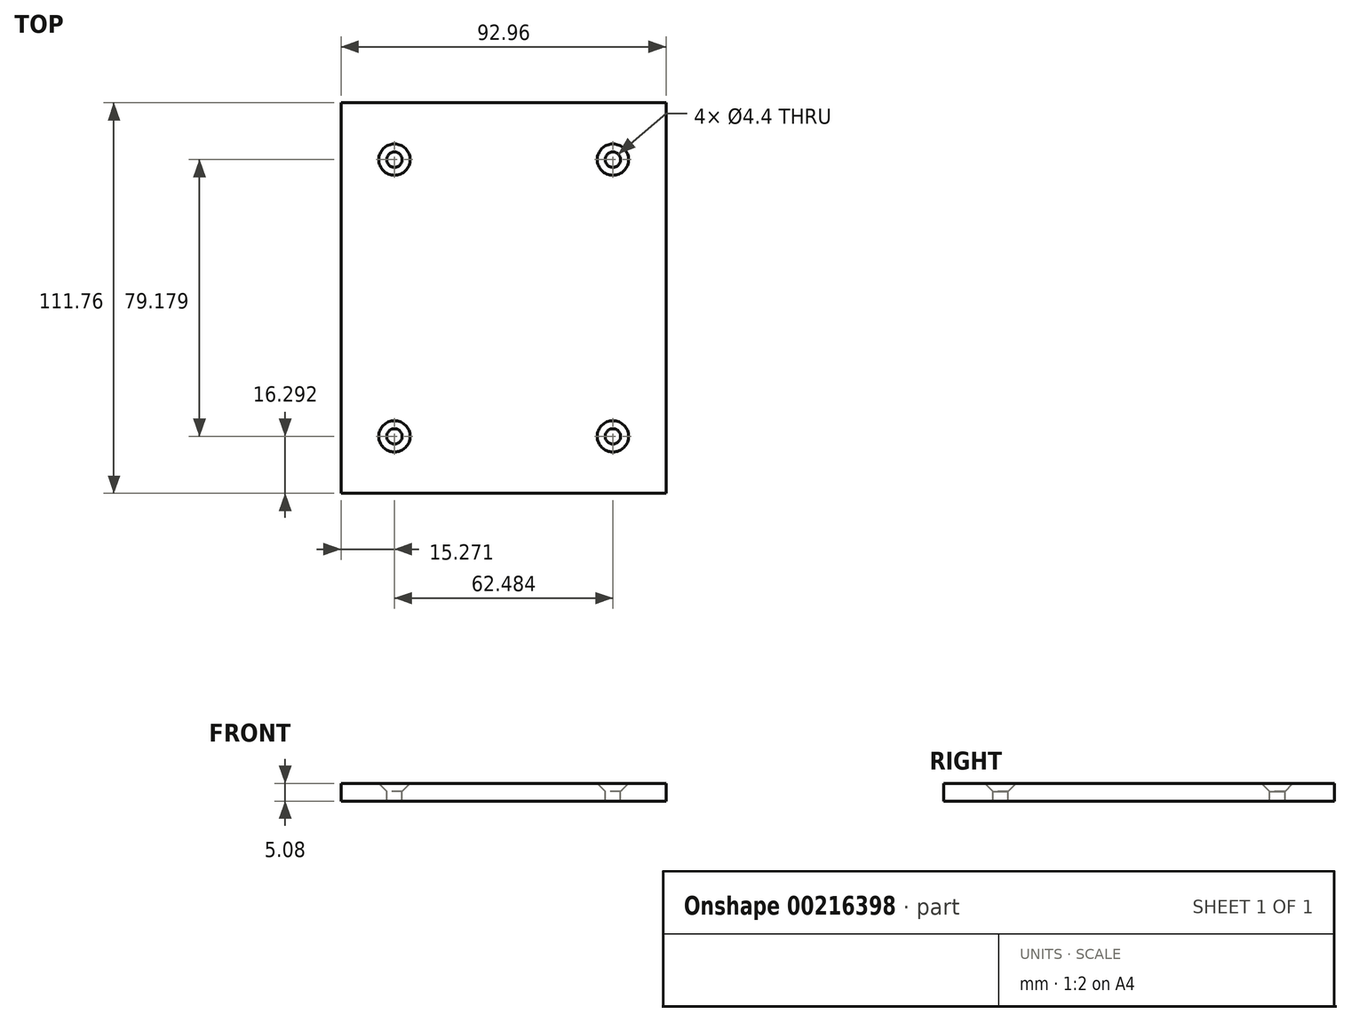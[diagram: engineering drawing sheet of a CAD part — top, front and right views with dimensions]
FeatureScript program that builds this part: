
annotation { "Feature Type Name" : "Feature", "Feature Type Description" : "" }
export const myFeature = defineFeature(function(context is Context, id is Id, definition is map)
    precondition{}
    {
        {
            var Q0;
            Q0=qCreatedBy(makeId("Top.planeOp"),FACE);
            var sketch = newSketch(context, id + "F0", { "sketchPlane" : qUnion([Q0])});
            skLineSegment(sketch, "E0.bottom", {"start": v(-46.48, 55.88) * mm, "end": v(46.48, 55.88) * mm});
            skLineSegment(sketch, "E0.top", {"start": v(-46.48, -55.88) * mm, "end": v(46.48, -55.88) * mm});
            skLineSegment(sketch, "E0.left", {"start": v(-46.48, 55.88) * mm, "end": v(-46.48, -55.88) * mm});
            skLineSegment(sketch, "E0.right", {"start": v(46.48, 55.88) * mm, "end": v(46.48, -55.88) * mm});
            skPoint(sketch, "E0.middle", {"position": v(0, 0) * mm});
            skSolve(sketch);
        }
        {
            var Q0;
            Q0 = qSketchRegion(id + "F0", true);
            extrude(context, id + "F1", {"entities" : qUnion([Q0]), "depth" : 5.08 * mm});
        }
        {
            var Q0;
            Q0=makeQuery(id+"F1.opExtrude","CAP_FACE",FACE,{"disambiguationData":[OSD([sQuery(id+"F0.wireOp",EDGE,"E0.bottom"),sQuery(id+"F0.wireOp",EDGE,"E0.top"),sQuery(id+"F0.wireOp",EDGE,"E0.left"),sQuery(id+"F0.wireOp",EDGE,"E0.right")])],"isStart":false});
            var sketch = newSketch(context, id + "F2", { "sketchPlane" : qUnion([Q0])});
            skPoint(sketch, "E1", {"position": v(-31.2, 39.6) * mm});
            skPoint(sketch, "E2.0.1.0", {"position": v(31.28, 39.6) * mm});
            skPoint(sketch, "E2.1.0.0", {"position": v(-31.2, -39.59) * mm});
            skPoint(sketch, "E2.1.1.0", {"position": v(31.28, -39.59) * mm});
            skPoint(sketch, "E2.2.0.0", {"position": v(-31.2, -118.77) * mm});
            skPoint(sketch, "E2.2.1.0", {"position": v(31.28, -118.77) * mm});
            skLineSegment(sketch, "E2.direction1", {"start": v(-31.2, 39.6) * mm, "end": v(-31.2, -39.59) * mm, "construction": true});
            skLineSegment(sketch, "E2.direction2", {"start": v(-31.2, 39.6) * mm, "end": v(31.28, 39.6) * mm, "construction": true});
            skSolve(sketch);
        }
        {
            var Q0;
            Q0=sQuery(id+"F2.wireOp",VERTEX,"E1");
            var Q1;
            Q1=sQuery(id+"F2.wireOp",VERTEX,"E2.1.0.0");
            var Q2;
            Q2=sQuery(id+"F2.wireOp",VERTEX,"E2.1.1.0");
            var Q3;
            Q3=sQuery(id+"F2.wireOp",VERTEX,"E2.0.1.0");
            var Q4;
            Q4=makeQuery(id+"F1.opExtrude","SWEPT_BODY",BODY,{"disambiguationData":[OSD([sQuery(id+"F0.wireOp",EDGE,"E0.bottom"),sQuery(id+"F0.wireOp",EDGE,"E0.top"),sQuery(id+"F0.wireOp",EDGE,"E0.left"),sQuery(id+"F0.wireOp",EDGE,"E0.right")])]});
            hole(context, id + "F3", {"style" : HoleStyle.C_SINK, "endStyle" : HoleEndStyle.BLIND, "standardTappedOrClearance" : lookupTablePath({ "standard" : "ISO", "fit" : "Normal", "size" : "M4", "type" : "Clearance" }), "standardBlindInLast" : lookupTablePath({ "fit" : "Standard", "standard" : "ISO", "size" : "M4", "type" : "Clearance" }), "holeDiameter" : 4.4 * mm, "cSinkDiameter" : 8.96 * mm, "cSinkAngle" : 90 * degree, "holeDepth" : 37.19 * mm, "tappedDepth" : 34.92 * mm, "tapClearance" : 3, "locations" : qUnion([Q0, Q1, Q2, Q3]), "scope" : qUnion([Q4])});
        }
    });
